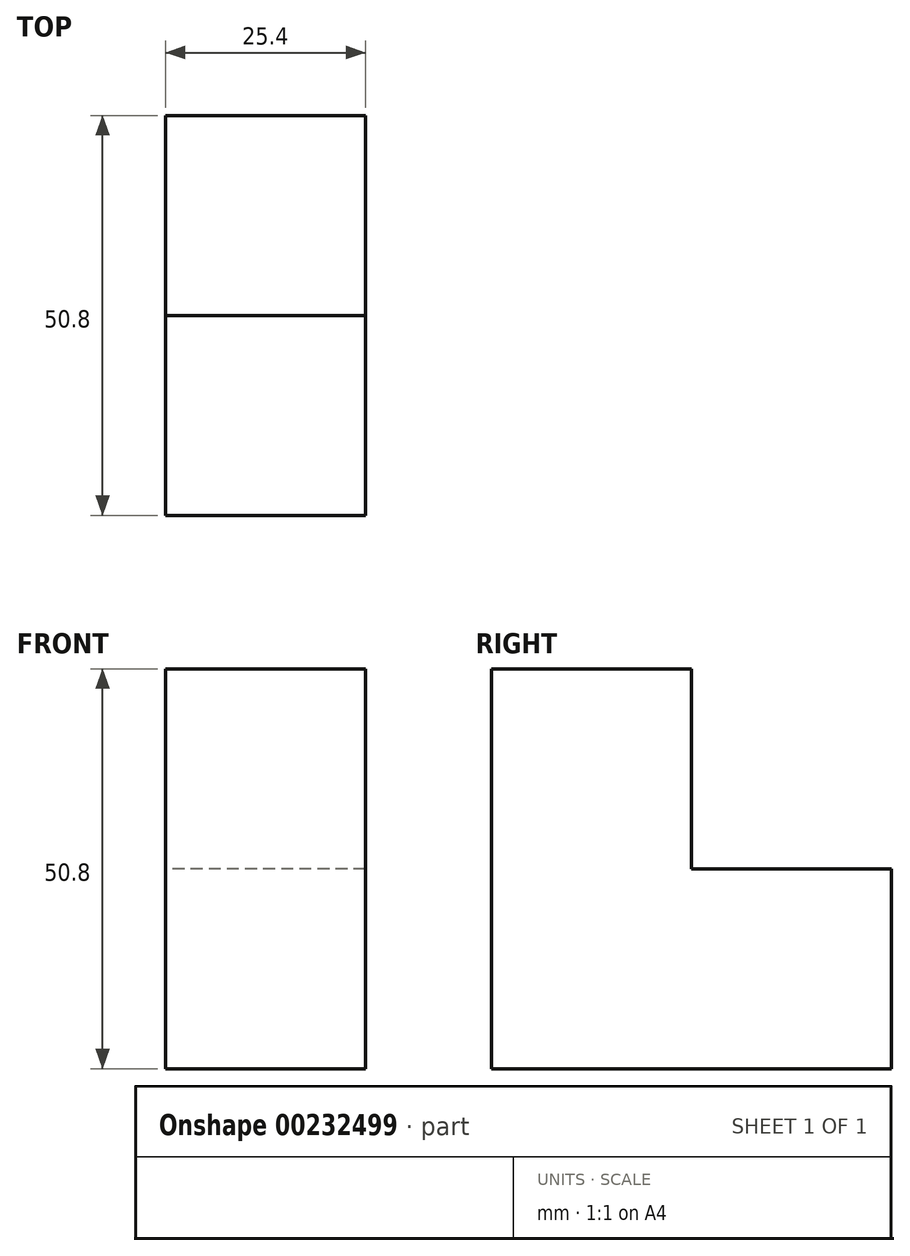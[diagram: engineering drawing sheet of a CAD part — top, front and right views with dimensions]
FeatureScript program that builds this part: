
annotation { "Feature Type Name" : "Feature", "Feature Type Description" : "" }
export const myFeature = defineFeature(function(context is Context, id is Id, definition is map)
    precondition{}
    {
        {
            var Q0;
            Q0=qCreatedBy(makeId("Right.planeOp"),FACE);
            var sketch = newSketch(context, id + "F0", { "sketchPlane" : qUnion([Q0])});
            skLineSegment(sketch, "E0.bottom", {"start": v(0, 0) * mm, "end": v(25.4, 0) * mm});
            skLineSegment(sketch, "E0.top", {"start": v(0, -50.8) * mm, "end": v(25.4, -50.8) * mm});
            skLineSegment(sketch, "E0.left", {"start": v(0, 0) * mm, "end": v(0, -50.8) * mm});
            skLineSegment(sketch, "E0.right", {"start": v(25.4, 0) * mm, "end": v(25.4, -50.8) * mm});
            skLineSegment(sketch, "E1.bottom", {"start": v(25.4, -50.8) * mm, "end": v(50.8, -50.8) * mm});
            skLineSegment(sketch, "E1.top", {"start": v(25.4, -25.4) * mm, "end": v(50.8, -25.4) * mm});
            skLineSegment(sketch, "E1.left", {"start": v(25.4, -50.8) * mm, "end": v(25.4, -25.4) * mm});
            skLineSegment(sketch, "E1.right", {"start": v(50.8, -50.8) * mm, "end": v(50.8, -25.4) * mm});
            skSolve(sketch);
        }
        {
            var Q0;
            Q0=makeQuery(id+"F0.imprint","IMPRINT",FACE,{"disambiguationData":[TD([[makeQuery(id+"F0.imprint","IMPRINT",EDGE,{"derivedFrom":sQuery(id+"F0.wireOp",EDGE,"E1.bottom")}),1.0]])]});
            var Q1;
            Q1=makeQuery(id+"F0.imprint","IMPRINT",FACE,{"disambiguationData":[TD([[makeQuery(id+"F0.imprint","IMPRINT",EDGE,{"derivedFrom":sQuery(id+"F0.wireOp",EDGE,"E0.bottom")}),-1.0]])]});
            extrude(context, id + "F1", {"entities" : qUnion([Q0, Q1]), "depth" : 25.4 * mm});
        }
    });
